# Revit family: Toilet_Seat-Round-American_Standard-SEATS-5503X_Series
name_source: partatom
category: Specialty Equipment
revit_build: Autodesk Revit 2018 (Build: 20170223_1515(x64)
units: mm (PartAtom-declared; Revit-internal decimal feet)

## family parameters
Always vertical = No
Cut with Voids When Loaded = No
OmniClass Number = 23.45.05.21.14.11
OmniClass Title = Water Closet Seats
Part Type = Normal
Room Calculation Point = No
Round Connector Dimension = Use Diameter
Shared = Yes
Work Plane-Based = Yes

## types (4) — shared parameters
760225-100.0070A Bottom Mounting Kit = No
760357-100.0070A Top Mounting Kit = No
Assembly Code = C1030200
Default Elevation = 0"
Height = 1 5/8"
Installation Type = Surface Mounted
Manufacturer = American Standard
Product Documentation Link = https://americanstandard.box.com
URL = http://www.americanstandard-us.com
Width = 14 3/16"

## per-type parameters (varying)
| type | Description | Finish | Length | Material | Model Type | Product Page URL |
| 5503A00B.020 | Transitional Slow-Close Elongated Toilet Seat | Plastic-American Standard-020-White | 17 1/4" | Plastic-American Standard-020-White | 5503A00B | https://www.americanstandard-us.com |
| 5503A00B.222 | Transitional Slow-Close Elongated Toilet Seat | Plastic-American Standard-222-Linen | 17 1/4" | Plastic-American Standard-222-Linen | 5503A00B | https://www.americanstandard-us.com |
| 5503A00B.021 | Transitional Slow-Close Elongated Toilet Seat | Plastic-American Standard-021-Bone | 17 1/4" | Plastic-American Standard-021-Bone | 5503A00B | https://www.americanstandard-us.com |
| 5503B00B.020 | Transitional Slow-Close Round Front Toilet Seat | Plastic-American Standard-020-White | 15 3/16" | Plastic-American Standard-020-White | 5503B00B | ahttps://www.americanstandard-us.com |

note: column(s) folded — value = type name in every type: Model

## geometry (parser evidence)
native form markers: Sweep x6
no freeform markers — native parametric forms only
